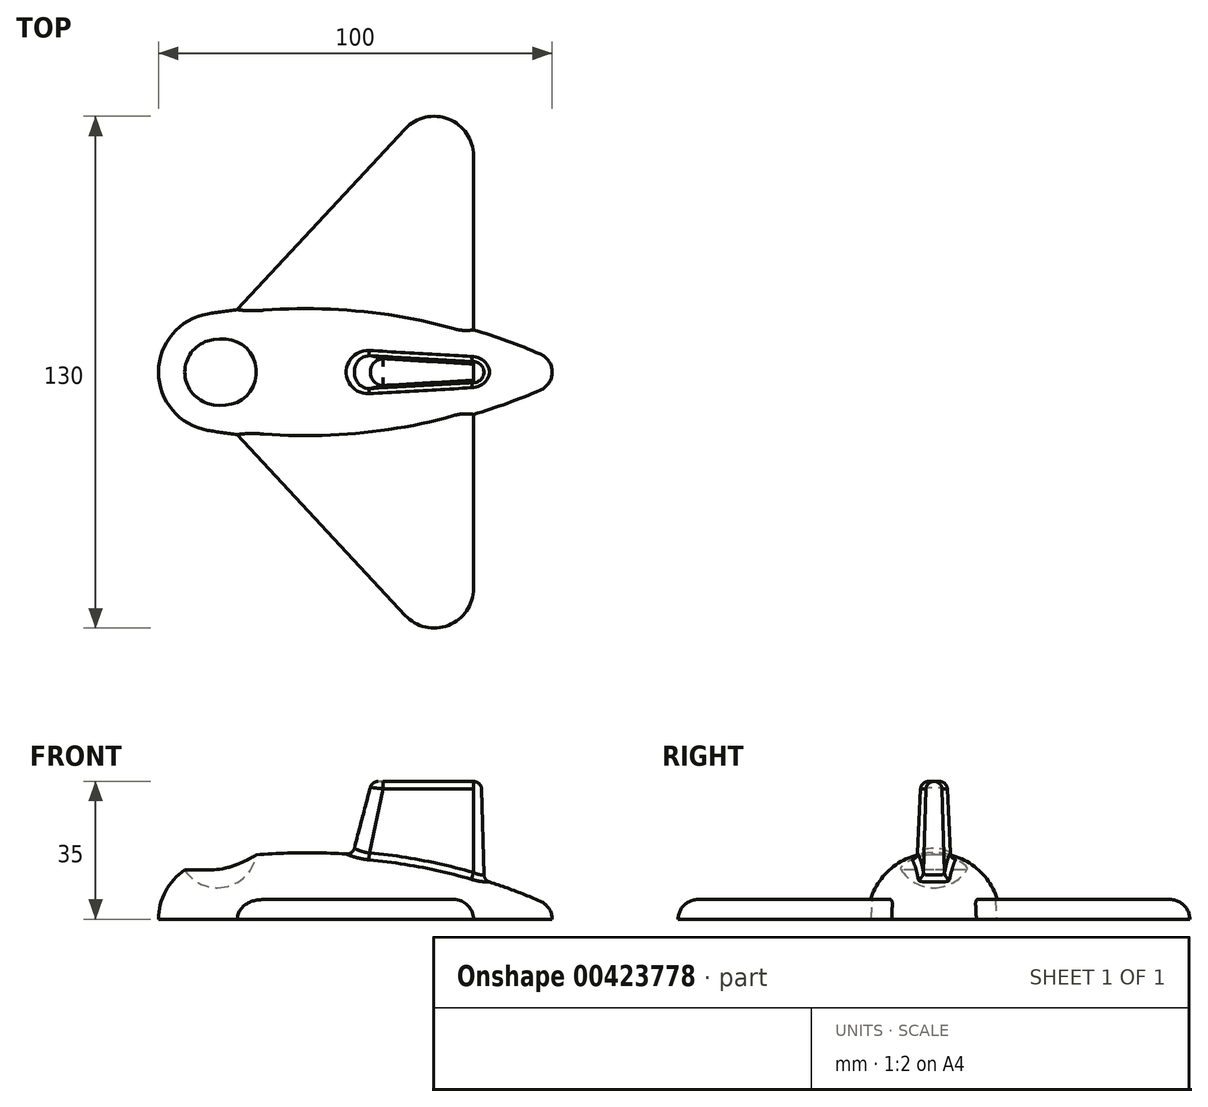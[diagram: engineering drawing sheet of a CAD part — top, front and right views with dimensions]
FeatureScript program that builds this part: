
annotation { "Feature Type Name" : "Feature", "Feature Type Description" : "" }
export const myFeature = defineFeature(function(context is Context, id is Id, definition is map)
    precondition{}
    {
        {
            var Q0;
            Q0=qCreatedBy(makeId("Top.planeOp"),FACE);
            var sketch = newSketch(context, id + "F0", { "sketchPlane" : qUnion([Q0])});
            skArc(sketch, "E0", {"start": v(-2.5, 14.8) * mm, "mid": v(-11.46, 9.68) * mm, "end": v(-15, 0) * mm});
            skLineSegment(sketch, "E1", {"start": v(-15, 0) * mm, "end": v(85, 0) * mm});
            skArc(sketch, "E2", {"start": v(85, 0) * mm, "mid": v(84.18, 2.75) * mm, "end": v(81.98, 4.6) * mm});
            skArc(sketch, "E3", {"start": v(81.98, 4.6) * mm, "mid": v(40.48, 15.8) * mm, "end": v(-2.5, 14.8) * mm});
            skSolve(sketch);
        }
        {
            var Q0;
            Q0=makeQuery(id+"F0.imprint","IMPRINT",FACE,{"disambiguationData":[TD([[makeQuery(id+"F0.imprint","IMPRINT",EDGE,{"derivedFrom":sQuery(id+"F0.wireOp",EDGE,"E0")}),1.0]])]});
            var Q1;
            Q1=sQuery(id+"F0.wireOp",EDGE,"E1");
            revolve(context, id + "F1", {"entities" : qUnion([Q0]), "axis" : qUnion([Q1]), "revolveType" : RevolveType.ONE_DIRECTION, "angle" : 180 * degree});
        }
        {
            var Q0;
            Q0=qCreatedBy(makeId("Front.planeOp"),FACE);
            var sketch = newSketch(context, id + "F2", { "sketchPlane" : qUnion([Q0])});
            skArc(sketch, "E4", {"start": v(0, 8) * mm, "mid": v(10, 18) * mm, "end": v(0, 28) * mm});
            skLineSegment(sketch, "E5", {"start": v(0, 28) * mm, "end": v(0, 8) * mm});
            skPoint(sketch, "E6.center.orphan", {"position": v(0, 0) * mm});
            skPoint(sketch, "E6.end.orphan", {"position": v(-15, 0) * mm});
            skSolve(sketch);
        }
        {
            var Q0;
            Q0=makeQuery(id+"F2.imprint","IMPRINT",FACE,{"disambiguationData":[TD([[makeQuery(id+"F2.imprint","IMPRINT",EDGE,{"derivedFrom":sQuery(id+"F2.wireOp",EDGE,"E4")}),1.0]])]});
            var Q1;
            Q1=sQuery(id+"F2.wireOp",EDGE,"E5");
            revolve(context, id + "F3", {"operationType" : NewBodyOperationType.REMOVE, "entities" : qUnion([Q0]), "axis" : qUnion([Q1]), "revolveType" : RevolveType.FULL, "oppositeDirection" : true});
        }
        {
            var Q0;
            Q0=qCreatedBy(makeId("Top.planeOp"),FACE);
            var sketch = newSketch(context, id + "F4", { "sketchPlane" : qUnion([Q0])});
            skArc(sketch, "E7", {"start": v(35.66, 4.96) * mm, "mid": v(30, 0) * mm, "end": v(35.66, -4.96) * mm});
            skArc(sketch, "E8", {"start": v(65, -3) * mm, "mid": v(68, 0) * mm, "end": v(65, 3) * mm});
            skLineSegment(sketch, "E9", {"start": v(65, -3) * mm, "end": v(35, -5) * mm});
            skLineSegment(sketch, "E10.MirrorCS", {"start": v(65, 3) * mm, "end": v(35, 5) * mm});
            skSolve(sketch);
        }
        {
            var Q0;
            Q0=qCreatedBy(makeId("Top.planeOp"),FACE);
            cPlane(context, id + "F5", {"entities" : qUnion([Q0]), "cplaneType" : CPlaneType.OFFSET, "offset" : 35 * mm, "width" : 150 * mm, "height" : 150 * mm});
        }
        {
            var Q0;
            Q0=qCreatedBy(id+"F5.planeOp",FACE);
            var sketch = newSketch(context, id + "F6", { "sketchPlane" : qUnion([Q0])});
            skPoint(sketch, "E11.0", {"position": v(65, 0) * mm});
            skArc(sketch, "E12", {"start": v(65, -2) * mm, "mid": v(67, 0) * mm, "end": v(65, 2) * mm});
            skArc(sketch, "E13", {"start": v(42.88, 3.28) * mm, "mid": v(39.2, 0) * mm, "end": v(42.88, -3.28) * mm});
            skLineSegment(sketch, "E14", {"start": v(65, -2) * mm, "end": v(42.5, -3.3) * mm});
            skLineSegment(sketch, "E15.MirrorCS", {"start": v(65, 2) * mm, "end": v(42.5, 3.3) * mm});
            skSolve(sketch);
        }
        {
            var Q1;
            {var subQ1=sQuery(id+"F6.wireOp",EDGE,"E12");Q1=makeQuery(id+"F6.imprint","IMPRINT",FACE,{"disambiguationData":[TD([[makeQuery(id+"F6.imprint","IMPRINT",EDGE,{"derivedFrom":subQ1}),1.0]])]});}
            var Q2;
            {var subQ4=sQuery(id+"F4.wireOp",EDGE,"E8");Q2=makeQuery(id+"F4.imprint","IMPRINT",FACE,{"disambiguationData":[TD([[makeQuery(id+"F4.imprint","IMPRINT",EDGE,{"derivedFrom":subQ4}),1.0]])]});}
            loft(context, id + "F7", {"operationType" : NewBodyOperationType.ADD, "sheetProfilesArray" : [{ "sheetProfileEntities" : qUnion([Q1]) }, { "sheetProfileEntities" : qUnion([Q2]) }]});
        }
        {
            var Q0;
            Q0=makeQuery(id+"F7.opLoft","MID_CAP_EDGE",EDGE,{"disambiguationData":[OSD([sQuery(id+"F6.wireOp",EDGE,"E13"),sQuery(id+"F6.wireOp",EDGE,"E14"),sQuery(id+"F6.wireOp",EDGE,"E15.MirrorCS")])],"capPos":0.0});
            var Q1;
            Q1=makeQuery(id+"F7.opLoft","MID_CAP_EDGE",EDGE,{"disambiguationData":[OSD([sQuery(id+"F6.wireOp",EDGE,"E12"),sQuery(id+"F6.wireOp",EDGE,"E13"),sQuery(id+"F6.wireOp",EDGE,"E14")])],"capPos":0.0});
            var Q2;
            Q2=makeQuery(id+"F7.opLoft","MID_CAP_EDGE",EDGE,{"disambiguationData":[OSD([sQuery(id+"F6.wireOp",EDGE,"E12"),sQuery(id+"F6.wireOp",EDGE,"E14"),sQuery(id+"F6.wireOp",EDGE,"E15.MirrorCS")])],"capPos":0.0});
            var Q3;
            Q3=makeQuery(id+"F7.opLoft","MID_CAP_EDGE",EDGE,{"disambiguationData":[OSD([sQuery(id+"F6.wireOp",EDGE,"E13"),sQuery(id+"F6.wireOp",EDGE,"E15.MirrorCS")])],"capPos":0.0});
            fillet(context, id + "F8", {"entities" : qUnion([Q0, Q1, Q2, Q3]), "radius" : 2 * mm, "tangentPropagation" : true, "allowEdgeOverflow" : false});
        }
        {
            var Q0;
            Q0=makeQuery(id+"F7.boolean.opBoolean","INTERSECT",EDGE,{"derivedFrom":[makeQuery(id+"F1.opRevolve","SWEPT_FACE",FACE,{"disambiguationData":[OSD([sQuery(id+"F0.wireOp",EDGE,"E3")])]}),makeQuery(id+"F7.opLoft","SWEPT_FACE",FACE,{"disambiguationData":[OSD([sQuery(id+"F4.wireOp",EDGE,"E7"),sQuery(id+"F4.wireOp",EDGE,"E8"),sQuery(id+"F4.wireOp",EDGE,"E9"),sQuery(id+"F6.wireOp",EDGE,"E12"),sQuery(id+"F6.wireOp",EDGE,"E13"),sQuery(id+"F6.wireOp",EDGE,"E14")])]})]});
            var Q1;
            Q1=makeQuery(id+"F7.boolean.opBoolean","INTERSECT",EDGE,{"derivedFrom":[makeQuery(id+"F1.opRevolve","SWEPT_FACE",FACE,{"disambiguationData":[OSD([sQuery(id+"F0.wireOp",EDGE,"E3")])]}),makeQuery(id+"F7.opLoft","SWEPT_FACE",FACE,{"disambiguationData":[OSD([sQuery(id+"F4.wireOp",EDGE,"E7"),sQuery(id+"F4.wireOp",EDGE,"E9"),sQuery(id+"F4.wireOp",EDGE,"E10.MirrorCS"),sQuery(id+"F6.wireOp",EDGE,"E13"),sQuery(id+"F6.wireOp",EDGE,"E14"),sQuery(id+"F6.wireOp",EDGE,"E15.MirrorCS")])]})]});
            var Q2;
            Q2=makeQuery(id+"F7.boolean.opBoolean","INTERSECT",EDGE,{"derivedFrom":[makeQuery(id+"F1.opRevolve","SWEPT_FACE",FACE,{"disambiguationData":[OSD([sQuery(id+"F0.wireOp",EDGE,"E3")])]}),makeQuery(id+"F7.opLoft","SWEPT_FACE",FACE,{"disambiguationData":[OSD([sQuery(id+"F4.wireOp",EDGE,"E8"),sQuery(id+"F4.wireOp",EDGE,"E9"),sQuery(id+"F4.wireOp",EDGE,"E10.MirrorCS"),sQuery(id+"F6.wireOp",EDGE,"E12"),sQuery(id+"F6.wireOp",EDGE,"E14"),sQuery(id+"F6.wireOp",EDGE,"E15.MirrorCS")])]})]});
            var Q3;
            Q3=makeQuery(id+"F7.boolean.opBoolean","INTERSECT",EDGE,{"derivedFrom":[makeQuery(id+"F1.opRevolve","SWEPT_FACE",FACE,{"disambiguationData":[OSD([sQuery(id+"F0.wireOp",EDGE,"E3")])]}),makeQuery(id+"F7.opLoft","SWEPT_FACE",FACE,{"disambiguationData":[OSD([sQuery(id+"F4.wireOp",EDGE,"E7"),sQuery(id+"F4.wireOp",EDGE,"E10.MirrorCS"),sQuery(id+"F6.wireOp",EDGE,"E13"),sQuery(id+"F6.wireOp",EDGE,"E15.MirrorCS")])]})]});
            fillet(context, id + "F9", {"entities" : qUnion([Q0, Q1, Q2, Q3]), "radius" : 2 * mm, "tangentPropagation" : true, "allowEdgeOverflow" : false});
        }
        {
            var Q0;
            Q0=qCreatedBy(makeId("Top.planeOp"),FACE);
            var sketch = newSketch(context, id + "F10", { "sketchPlane" : qUnion([Q0])});
            skLineSegment(sketch, "E16", {"start": v(5, 15.86) * mm, "end": v(47.67, 61.8) * mm});
            skLineSegment(sketch, "E17", {"start": v(65, 55) * mm, "end": v(65, 10.74) * mm});
            skPoint(sketch, "E18.end.orphan", {"position": v(1.2, 11.78) * mm});
            skPoint(sketch, "E19.visualSharp", {"position": v(65, 80.46) * mm});
            skArc(sketch, "E19.filletArc", {"start": v(65, 55) * mm, "mid": v(58.66, 64.3) * mm, "end": v(47.67, 61.8) * mm});
            skLineSegment(sketch, "E20.MirrorCS", {"start": v(5, -15.86) * mm, "end": v(47.67, -61.8) * mm});
            skArc(sketch, "E21.MirrorCS", {"start": v(65, -55) * mm, "mid": v(58.66, -64.3) * mm, "end": v(47.67, -61.8) * mm});
            skLineSegment(sketch, "E22.MirrorCS", {"start": v(65, -55) * mm, "end": v(65, -10.74) * mm});
            skPoint(sketch, "E23.orphan", {"position": v(-2.5, 14.8) * mm});
            skPoint(sketch, "E24.orphan", {"position": v(81.98, 4.6) * mm});
            skPoint(sketch, "E25.orphan", {"position": v(-2.5, -14.8) * mm});
            skPoint(sketch, "E26.orphan", {"position": v(81.98, -4.6) * mm});
            skLineSegment(sketch, "E27", {"start": v(5, 15.86) * mm, "end": v(5, 13.01) * mm});
            skLineSegment(sketch, "E28", {"start": v(5, 13.01) * mm, "end": v(64.98, 8.5) * mm});
            skLineSegment(sketch, "E29", {"start": v(64.98, 8.5) * mm, "end": v(65, 10.74) * mm});
            skLineSegment(sketch, "E30", {"start": v(5, -15.86) * mm, "end": v(6, -11.41) * mm});
            skLineSegment(sketch, "E31", {"start": v(6, -11.41) * mm, "end": v(64.13, -7.38) * mm});
            skLineSegment(sketch, "E32", {"start": v(64.13, -7.38) * mm, "end": v(65, -10.74) * mm});
            skSolve(sketch);
        }
        {
            var Q0;
            Q0=makeQuery(id+"F10.imprint","IMPRINT",FACE,{"disambiguationData":[TD([[makeQuery(id+"F10.imprint","IMPRINT",EDGE,{"derivedFrom":sQuery(id+"F10.wireOp",EDGE,"E16")}),-1.0]])]});
            var Q1;
            Q1=makeQuery(id+"F10.imprint","IMPRINT",FACE,{"disambiguationData":[TD([[makeQuery(id+"F10.imprint","IMPRINT",EDGE,{"derivedFrom":sQuery(id+"F10.wireOp",EDGE,"E20.MirrorCS")}),1.0]])]});
            extrude(context, id + "F11", {"entities" : qUnion([Q0, Q1]), "operationType" : NewBodyOperationType.ADD, "depth" : 5 * mm});
        }
        {
            var Q0;
            Q0=makeQuery(id+"F11.opExtrude","CAP_EDGE",EDGE,{"disambiguationData":[OSD([sQuery(id+"F10.wireOp",EDGE,"E20.MirrorCS")])],"isStart":false});
            var Q1;
            Q1=makeQuery(id+"F11.opExtrude","CAP_EDGE",EDGE,{"disambiguationData":[OSD([sQuery(id+"F10.wireOp",EDGE,"E16")])],"isStart":false});
            fillet(context, id + "F12", {"entities" : qUnion([Q0, Q1]), "radius" : 5 * mm, "tangentPropagation" : true, "allowEdgeOverflow" : false});
        }
    });
